# Revit family: AnchorPoint_Kattsafe_Rapid_TopMount
name_source: partatom
category: Specialty Equipment
units: mm (PartAtom-declared; Revit-internal decimal feet)

## family parameters
Cut with Voids When Loaded = No
Enable Cutting in Views = No
Host = Face
Maintain Annotation Orientation = No
OmniClass Number = 23.27.71.21
Part Type = Normal
Room Calculation Point = No
Round Connector Dimension = Use Diameter
Shared = No

## types (2) — shared parameters
Assembly Code = E1090100
Description = Our Kattsafe anchor points are specifically designed, manufactured, and tested to comply with and often exceed Australian Standards, effectively handling excessive loads and saving lives when using a harness and lanyard system.
ElementType = Fall Protection
Export Type to IFC As = IfcBuildingElementProxy
IfcExportAs = IfcBuildingElementProxy
IfcExportType = USERDEFINED
Manufacturer = Kattsafe®
ManufacturerOverallDepth = 288 mm  [stored 0.944882 ft]
ManufacturerOverallHeight = 48 mm  [stored 0.15748 ft]
ManufacturerURLProductSpecific = https://kattsafe.com.au
Material = Aluminum_Kattsafe_Satin
ModifiedIssue = 20240430 $
Type IFC Predefined Type = USERDEFINED
URL = https://kattsafe.com.au
Uniclass2015Code = Pr_40_70_75_75
Uniclass2015Title = Safety access anchor devices
Uniclass2015Version = Products v1.23
zero-valued in all types: Default Elevation

## per-type parameters (varying)
| type | ManufacturerOverallWidth | ManufacturerSpecCode | Model | StandardMount | StandardVoidDepth | Type Comments | WideDeckMount | WideVoidDepth |
| Standard (AP135A) | 250 mm  [stored 0.82021 ft] | AP135A | AP135A | Yes | 32 mm  [stored 0.104987 ft] | Top Mount Anchor | No | 1 mm  [stored 0.00328084 ft] |
| Wide Deck (AP135W) | 432 mm  [stored 1.41732 ft] | AP135W | AP135W | No | 1 mm  [stored 0.00328084 ft] | Top Mount Anchor - Wide Deck | Yes | 32 mm  [stored 0.104987 ft] |

note: [stored X ft] marks values corroborated as IEEE doubles in the binary element streams (Revit-internal decimal feet)

## geometry (parser evidence)
native form markers: Sweep x1
no freeform markers — native parametric forms only
